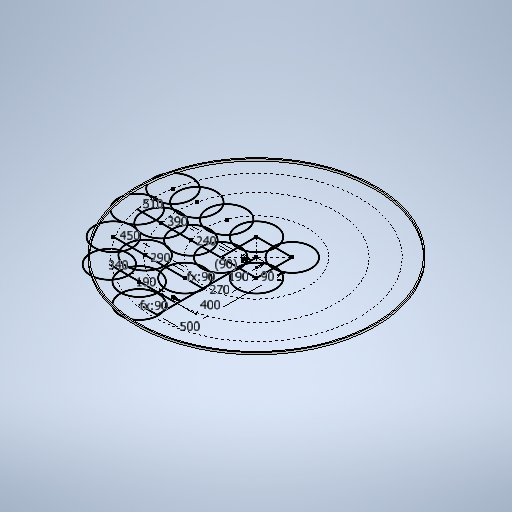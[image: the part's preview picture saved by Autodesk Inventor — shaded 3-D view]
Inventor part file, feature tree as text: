
AUTODESK INVENTOR PART (.ipt)
format: ipt  version: 2025.1 (Build 291241020, 241B)  size: 314,880 bytes
history: native  units: mm
features: sketch x3, extrude x1
ambient origin geometry x8: Origin, YZ Plane, XZ Plane, XY Plane, X Axis, Y Axis, Z Axis, Center Point
bodies: Solid1 (feature_tree)
feature tree (4):
  extrude  "Extrusion1"  Depth=6.0mm
  sketch  "Sketch2"  dims[d2=10.0mm d3=0.0mm]
  sketch  "Sketch3"  dims[d4=190.0mm d7=90.0mm d8=270.0mm d9=400.0mm d10=500.0mm d11=240.0mm d12=390.0mm d13=510.0mm d14=90.0mm d15=90.0mm d16=290.0mm d17=450.0mm d18=190.0mm d19=340.0mm d20=90.0mm d21=190.0mm d22=1200.0mm]
  sketch  "Sketch1"  dims[d0=1200.0mm d1=6.0mm]
